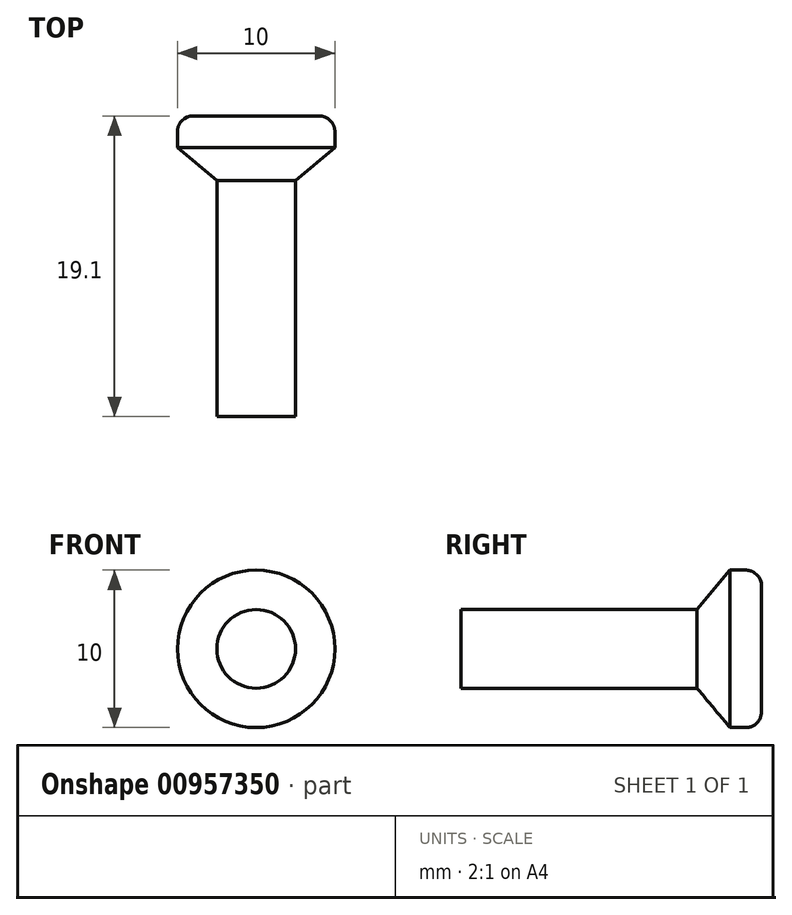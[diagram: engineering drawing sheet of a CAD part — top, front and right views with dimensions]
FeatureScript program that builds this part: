
annotation { "Feature Type Name" : "Feature", "Feature Type Description" : "" }
export const myFeature = defineFeature(function(context is Context, id is Id, definition is map)
    precondition{}
    {
        {
            var Q0;
            Q0=qCreatedBy(makeId("Top.planeOp"),FACE);
            var sketch = newSketch(context, id + "F0", { "sketchPlane" : qUnion([Q0])});
            skLineSegment(sketch, "E0", {"start": v(0, 0) * mm, "end": v(0, 19.1) * mm});
            skLineSegment(sketch, "E1", {"start": v(0, 19.1) * mm, "end": v(4, 19.1) * mm});
            skLineSegment(sketch, "E2", {"start": v(5, 18.1) * mm, "end": v(5, 17.1) * mm});
            skLineSegment(sketch, "E3", {"start": v(5, 17.1) * mm, "end": v(2.5, 15) * mm});
            skLineSegment(sketch, "E4", {"start": v(2.5, 15) * mm, "end": v(2.5, 0) * mm});
            skLineSegment(sketch, "E5", {"start": v(2.5, 0) * mm, "end": v(0, 0) * mm});
            skPoint(sketch, "E6.visualSharp", {"position": v(5, 19.1) * mm});
            skArc(sketch, "E6.filletArc", {"start": v(5, 18.1) * mm, "mid": v(4.7, 18.8) * mm, "end": v(4, 19.1) * mm});
            skSolve(sketch);
        }
        {
            var Q0;
            Q0=makeQuery(id+"F0.imprint","IMPRINT",FACE,{"disambiguationData":[TD([[makeQuery(id+"F0.imprint","IMPRINT",EDGE,{"derivedFrom":sQuery(id+"F0.wireOp",EDGE,"E0")}),-1.0]])]});
            var Q1;
            Q1=sQuery(id+"F0.wireOp",EDGE,"E0");
            revolve(context, id + "F1", {"surfaceOperationType" : NewSurfaceOperationType.NEW, "entities" : qUnion([Q0]), "axis" : qUnion([Q1]), "revolveType" : RevolveType.FULL});
        }
    });
